# Revit family: P200921MX-034c_MFW2055FRZ
name_source: partatom
category: Specialty Equipment
units: mm (PartAtom-declared; Revit-internal decimal feet)

## family parameters
Always vertical = Yes
Cut with Voids When Loaded = No
Enable Cutting in Views = No
Maintain Annotation Orientation = No
Part Type = Normal
Room Calculation Point = No
Round Connector Dimension = Use Diameter
Shared = No
Work Plane-Based = No

## types (1)
- MFW2055FRZ
    Accent Material = ARCAT - Metal - Steel -Gray
    Amps = 0 A
    Body Material = ARCAT - Metal - Steel -Gray
    Clearance Material = ARCAT - Clearance
    Default Elevation = 0"
    Depth = 34 3/8"
    Description = 30-Inch Wide French Door Refrigerator with Exterior Water Dispenser- 20 Cu. Ft.
Réfrigérateur à portes françaises Maytag® avec distributeur d’eau extérieur, 30 po, 20 pi3
    Dimension Guide = http://access.whirlpool.com Guide&sku=MFW2055FRZ&language=EN
http://access.whirlpool.com Guide&sku=MFW2055FRZ&language=EN
    Display Panel Material = ARCAT - Glass - Tempered - Black
    Door Material = ARCAT - Metal - Steel - Stainless
    Energy Guide = http://access.whirlpool.com Guide&sku=MFW2055FRZ&language=EN
http://access.whirlpool.com Guide&sku=MFW2055FRZ&language=FR
    Family Name = Refrigeration
    Feature 1 = Fingerprint Resistant Stainless Steel
Acier inoxydable résistant aux traces de doigts
    Feature 2 = Temperature-Controlled Wide-N-Fresh™ Deli Drawer
Tiroir à charcuterie à température contrôlée Wide-N-Fresh™
    Feature 3 = BrightSeries™ LED Lighting
Éclairage à DEL BrightSeries™
    Handle Material = ARCAT - Metal - Steel -Gray - Light
    Height = 68 3/8"
    Manufacturer = Maytag
    Model = MFW2055FRZ
    Voltage = 0 V
    Wheel Material = ARCAT - Metal - Steel -Gray
    Width = 30 1/8"

## geometry (parser evidence)
native form markers: Sweep x4
no freeform markers — native parametric forms only
